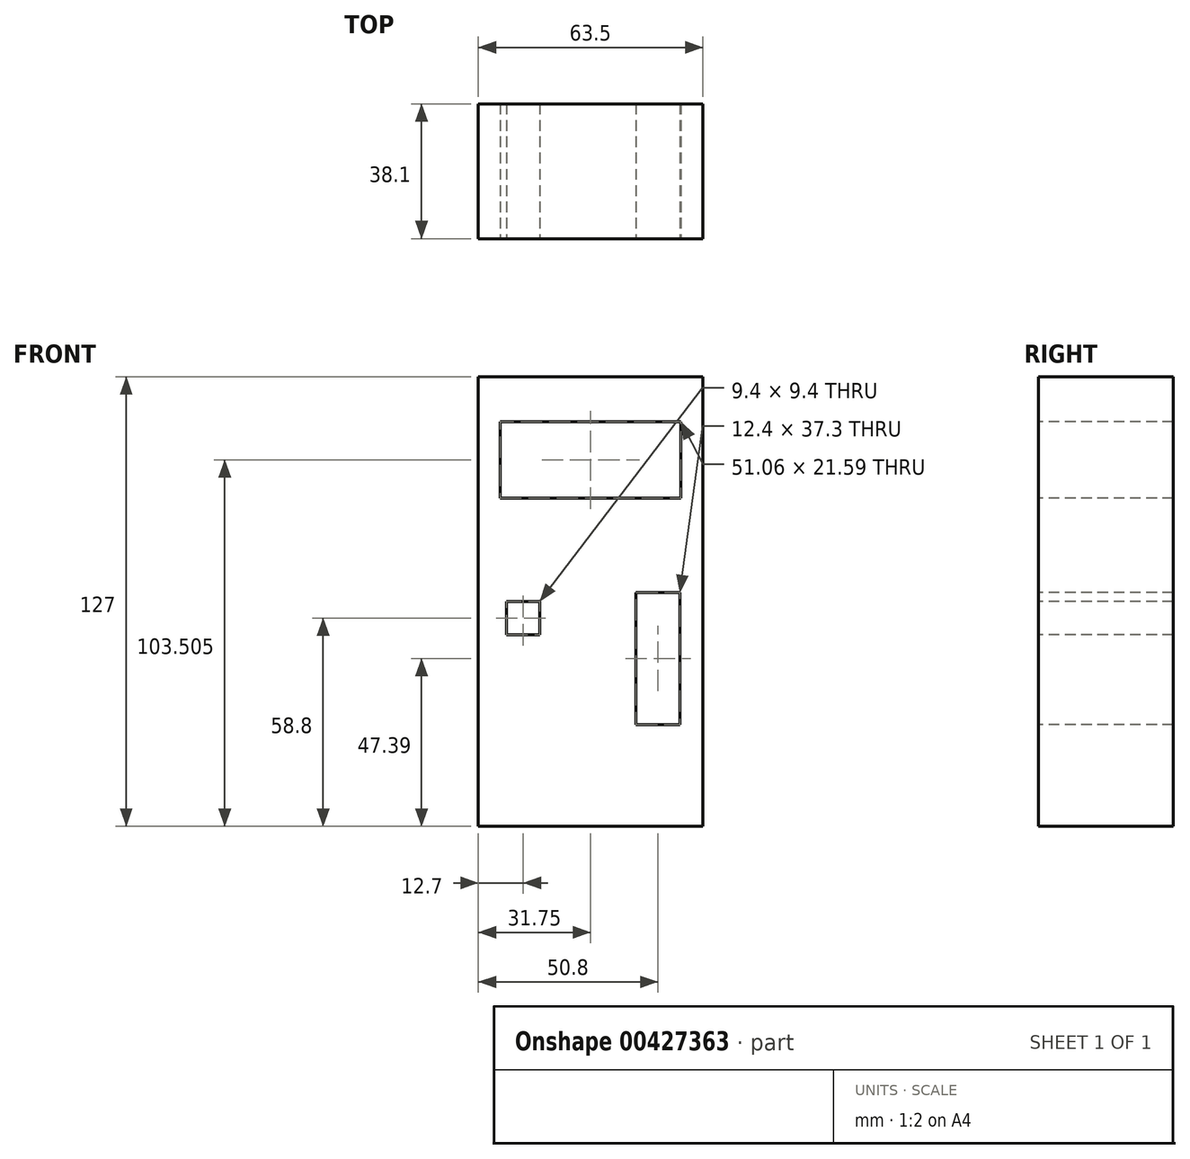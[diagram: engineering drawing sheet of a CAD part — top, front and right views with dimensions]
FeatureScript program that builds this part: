
annotation { "Feature Type Name" : "Feature", "Feature Type Description" : "" }
export const myFeature = defineFeature(function(context is Context, id is Id, definition is map)
    precondition{}
    {
        {
            var Q0;
            Q0=qCreatedBy(makeId("Front.planeOp"),FACE);
            var sketch = newSketch(context, id + "F0", { "sketchPlane" : qUnion([Q0])});
            skLineSegment(sketch, "E0.bottom", {"start": v(-31.75, 63.5) * mm, "end": v(31.75, 63.5) * mm});
            skLineSegment(sketch, "E0.top", {"start": v(-31.75, -63.5) * mm, "end": v(31.75, -63.5) * mm});
            skLineSegment(sketch, "E0.left", {"start": v(-31.75, 63.5) * mm, "end": v(-31.75, -63.5) * mm});
            skLineSegment(sketch, "E0.right", {"start": v(31.75, 63.5) * mm, "end": v(31.75, -63.5) * mm});
            skLineSegment(sketch, "E1.bottom", {"start": v(-25.53, 50.8) * mm, "end": v(25.53, 50.8) * mm});
            skLineSegment(sketch, "E1.top", {"start": v(-25.53, 29.21) * mm, "end": v(25.53, 29.21) * mm});
            skLineSegment(sketch, "E1.left", {"start": v(-25.53, 50.8) * mm, "end": v(-25.53, 29.21) * mm});
            skLineSegment(sketch, "E1.right", {"start": v(25.53, 50.8) * mm, "end": v(25.53, 29.21) * mm});
            skLineSegment(sketch, "E2", {"start": v(0, 63.5) * mm, "end": v(0, -63.5) * mm, "construction": true});
            skLineSegment(sketch, "E3", {"start": v(-25.53, 40) * mm, "end": v(25.53, 40) * mm, "construction": true});
            skPoint(sketch, "E4", {"position": v(0, 40) * mm});
            skLineSegment(sketch, "E5", {"start": v(19.05, -63.5) * mm, "end": v(19.05, 63.5) * mm, "construction": true});
            skLineSegment(sketch, "E6.bottom", {"start": v(-14.35, 0) * mm, "end": v(-23.75, 0) * mm});
            skLineSegment(sketch, "E6.top", {"start": v(-14.35, -9.4) * mm, "end": v(-23.75, -9.4) * mm});
            skLineSegment(sketch, "E6.left", {"start": v(-14.35, 0) * mm, "end": v(-14.35, -9.4) * mm});
            skLineSegment(sketch, "E6.right", {"start": v(-23.75, 0) * mm, "end": v(-23.75, -9.4) * mm});
            skPoint(sketch, "E6.middle", {"position": v(-19.05, -4.7) * mm});
            skLineSegment(sketch, "E7.bottom", {"start": v(12.85, 2.54) * mm, "end": v(25.25, 2.54) * mm});
            skLineSegment(sketch, "E7.top", {"start": v(12.85, -34.76) * mm, "end": v(25.25, -34.76) * mm});
            skLineSegment(sketch, "E7.left", {"start": v(12.85, 2.54) * mm, "end": v(12.85, -34.76) * mm});
            skLineSegment(sketch, "E7.right", {"start": v(25.25, 2.54) * mm, "end": v(25.25, -34.76) * mm});
            skPoint(sketch, "E7.middle", {"position": v(19.05, -16.1) * mm});
            skSolve(sketch);
        }
        {
            var Q0;
            Q0=makeQuery(id+"F0.imprint","IMPRINT",FACE,{"disambiguationData":[TD([[makeQuery(id+"F0.imprint","IMPRINT",EDGE,{"derivedFrom":sQuery(id+"F0.wireOp",EDGE,"E0.bottom")}),-1.0]])]});
            var Q1;
            Q1=makeQuery(id+"F0.imprint","IMPRINT",FACE,{"disambiguationData":[TD([[makeQuery(id+"F0.imprint","IMPRINT",EDGE,{"derivedFrom":sQuery(id+"F0.wireOp",EDGE,"E1.bottom")}),1.0]])]});
            extrude(context, id + "F1", {"entities" : qUnion([Q0, Q1]), "oppositeDirection" : true, "depth" : 1 / 203.2 * mm, "offsetDistance" : 25.4 * mm});
        }
        {
            var Q0;
            Q0=makeQuery(id+"F1.opExtrude","CAP_FACE",FACE,{"disambiguationData":[OSD([sQuery(id+"F0.wireOp",EDGE,"E0.bottom"),sQuery(id+"F0.wireOp",EDGE,"E0.top"),sQuery(id+"F0.wireOp",EDGE,"E0.left"),sQuery(id+"F0.wireOp",EDGE,"E0.right"),sQuery(id+"F0.wireOp",EDGE,"E1.bottom"),sQuery(id+"F0.wireOp",EDGE,"E1.top"),sQuery(id+"F0.wireOp",EDGE,"E1.left"),sQuery(id+"F0.wireOp",EDGE,"E1.right"),sQuery(id+"F0.wireOp",EDGE,"E6.bottom"),sQuery(id+"F0.wireOp",EDGE,"E6.top"),sQuery(id+"F0.wireOp",EDGE,"E6.left"),sQuery(id+"F0.wireOp",EDGE,"E6.right"),sQuery(id+"F0.wireOp",EDGE,"E7.bottom"),sQuery(id+"F0.wireOp",EDGE,"E7.top"),sQuery(id+"F0.wireOp",EDGE,"E7.left"),sQuery(id+"F0.wireOp",EDGE,"E7.right")])],"isStart":false});
            var sketch = newSketch(context, id + "F2", { "sketchPlane" : qUnion([Q0])});
            skLineSegment(sketch, "E8", {"start": v(-31.75, 60.42) * mm, "end": v(31.75, 60.43) * mm, "construction": true});
            skLineSegment(sketch, "E9", {"start": v(-28.68, 63.5) * mm, "end": v(-28.67, -63.5) * mm, "construction": true});
            skLineSegment(sketch, "E10", {"start": v(-31.75, -60.42) * mm, "end": v(31.75, -60.42) * mm, "construction": true});
            skLineSegment(sketch, "E11", {"start": v(28.67, 63.5) * mm, "end": v(28.68, -63.5) * mm, "construction": true});
            skLineSegment(sketch, "E12", {"start": v(21.75, -60.42) * mm, "end": v(21.75, -63.5) * mm, "construction": true});
            skLineSegment(sketch, "E13", {"start": v(28.68, -53.5) * mm, "end": v(31.75, -53.5) * mm, "construction": true});
            skLineSegment(sketch, "E14", {"start": v(-21.75, -60.42) * mm, "end": v(-21.75, -63.5) * mm, "construction": true});
            skLineSegment(sketch, "E15", {"start": v(-31.75, -53.5) * mm, "end": v(-28.67, -53.5) * mm, "construction": true});
            skLineSegment(sketch, "E16", {"start": v(28.67, 53.5) * mm, "end": v(31.75, 53.5) * mm, "construction": true});
            skLineSegment(sketch, "E17", {"start": v(21.75, 63.5) * mm, "end": v(21.75, 60.43) * mm, "construction": true});
            skLineSegment(sketch, "E18", {"start": v(-21.75, 63.5) * mm, "end": v(-21.75, 60.42) * mm, "construction": true});
            skLineSegment(sketch, "E19", {"start": v(-31.75, 53.5) * mm, "end": v(-28.68, 53.5) * mm, "construction": true});
            skLineSegment(sketch, "E20", {"start": v(-7.25, 63.5) * mm, "end": v(-7.25, 60.42) * mm, "construction": true});
            skLineSegment(sketch, "E21", {"start": v(7.25, 63.5) * mm, "end": v(7.25, 60.42) * mm, "construction": true});
            skLineSegment(sketch, "E22", {"start": v(-21.75, 61.96) * mm, "end": v(-7.25, 61.96) * mm, "construction": true});
            skLineSegment(sketch, "E23", {"start": v(-7.25, 61.96) * mm, "end": v(7.25, 61.96) * mm, "construction": true});
            skLineSegment(sketch, "E24", {"start": v(7.25, 61.96) * mm, "end": v(21.75, 61.96) * mm, "construction": true});
            skLineSegment(sketch, "E25", {"start": v(-7.25, -60.42) * mm, "end": v(-7.25, -63.5) * mm, "construction": true});
            skLineSegment(sketch, "E26", {"start": v(7.25, -60.42) * mm, "end": v(7.25, -63.5) * mm, "construction": true});
            skLineSegment(sketch, "E27", {"start": v(-21.75, -61.96) * mm, "end": v(-7.25, -61.96) * mm, "construction": true});
            skLineSegment(sketch, "E28", {"start": v(-7.25, -61.96) * mm, "end": v(7.25, -61.96) * mm, "construction": true});
            skLineSegment(sketch, "E29", {"start": v(7.25, -61.96) * mm, "end": v(21.75, -61.96) * mm, "construction": true});
            skLineSegment(sketch, "E30", {"start": v(-31.75, 32.1) * mm, "end": v(-28.68, 32.1) * mm, "construction": true});
            skLineSegment(sketch, "E31", {"start": v(-31.75, 10.7) * mm, "end": v(-28.67, 10.7) * mm, "construction": true});
            skLineSegment(sketch, "E32", {"start": v(-31.75, -10.7) * mm, "end": v(-28.67, -10.7) * mm, "construction": true});
            skLineSegment(sketch, "E33", {"start": v(-31.75, -32.1) * mm, "end": v(-28.67, -32.1) * mm, "construction": true});
            skLineSegment(sketch, "E34", {"start": v(-30.21, 53.5) * mm, "end": v(-30.21, 32.1) * mm, "construction": true});
            skLineSegment(sketch, "E35", {"start": v(-30.21, 32.1) * mm, "end": v(-30.21, 10.7) * mm, "construction": true});
            skLineSegment(sketch, "E36", {"start": v(-30.21, 10.7) * mm, "end": v(-30.21, -10.7) * mm, "construction": true});
            skLineSegment(sketch, "E37", {"start": v(-30.21, -10.7) * mm, "end": v(-30.21, -32.1) * mm, "construction": true});
            skLineSegment(sketch, "E38", {"start": v(-30.21, -32.1) * mm, "end": v(-30.21, -53.5) * mm, "construction": true});
            skLineSegment(sketch, "E39", {"start": v(28.67, 32.1) * mm, "end": v(31.75, 32.1) * mm, "construction": true});
            skLineSegment(sketch, "E40", {"start": v(28.68, 10.7) * mm, "end": v(31.75, 10.7) * mm, "construction": true});
            skLineSegment(sketch, "E41", {"start": v(28.68, -10.7) * mm, "end": v(31.75, -10.7) * mm, "construction": true});
            skLineSegment(sketch, "E42", {"start": v(28.68, -32.1) * mm, "end": v(31.75, -32.1) * mm, "construction": true});
            skLineSegment(sketch, "E43", {"start": v(30.21, 53.5) * mm, "end": v(30.21, 32.1) * mm, "construction": true});
            skLineSegment(sketch, "E44", {"start": v(30.21, 32.1) * mm, "end": v(30.21, 10.7) * mm, "construction": true});
            skLineSegment(sketch, "E45", {"start": v(30.21, 10.7) * mm, "end": v(30.21, -10.7) * mm, "construction": true});
            skLineSegment(sketch, "E46", {"start": v(30.21, -10.7) * mm, "end": v(30.21, -32.1) * mm, "construction": true});
            skLineSegment(sketch, "E47", {"start": v(30.21, -32.1) * mm, "end": v(30.21, -53.5) * mm, "construction": true});
            skLineSegment(sketch, "E48", {"start": v(-31.75, 53.4) * mm, "end": v(-28.68, 53.4) * mm});
            skLineSegment(sketch, "E49", {"start": v(-28.68, 53.4) * mm, "end": v(-28.68, 60.42) * mm});
            skLineSegment(sketch, "E50", {"start": v(-28.68, 60.42) * mm, "end": v(-21.65, 60.42) * mm});
            skLineSegment(sketch, "E51", {"start": v(-21.65, 60.42) * mm, "end": v(-21.65, 63.5) * mm});
            skLineSegment(sketch, "E52", {"start": v(-21.65, 60.42) * mm, "end": v(-7.35, 60.42) * mm});
            skLineSegment(sketch, "E53", {"start": v(-7.35, 60.42) * mm, "end": v(-7.35, 63.5) * mm});
            skLineSegment(sketch, "E54", {"start": v(-7.35, 63.5) * mm, "end": v(7.35, 63.5) * mm});
            skLineSegment(sketch, "E55", {"start": v(7.35, 63.5) * mm, "end": v(7.35, 60.42) * mm});
            skLineSegment(sketch, "E56", {"start": v(7.35, 60.42) * mm, "end": v(21.65, 60.43) * mm});
            skLineSegment(sketch, "E57", {"start": v(21.65, 60.42) * mm, "end": v(21.65, 63.5) * mm});
            skLineSegment(sketch, "E58", {"start": v(21.65, 60.43) * mm, "end": v(28.67, 60.43) * mm});
            skLineSegment(sketch, "E59", {"start": v(28.67, 60.43) * mm, "end": v(28.67, 53.4) * mm});
            skLineSegment(sketch, "E60", {"start": v(28.67, 53.4) * mm, "end": v(31.75, 53.4) * mm});
            skLineSegment(sketch, "E61", {"start": v(-21.65, 63.5) * mm, "end": v(-7.35, 63.5) * mm});
            skLineSegment(sketch, "E62", {"start": v(7.35, 63.5) * mm, "end": v(21.65, 63.5) * mm});
            skLineSegment(sketch, "E63", {"start": v(-31.75, 53.4) * mm, "end": v(-31.75, 32.2) * mm});
            skLineSegment(sketch, "E64", {"start": v(-31.75, 32.2) * mm, "end": v(-28.68, 32.2) * mm});
            skLineSegment(sketch, "E65", {"start": v(-28.68, 32.2) * mm, "end": v(-28.68, 53.4) * mm});
            skLineSegment(sketch, "E66", {"start": v(-31.75, 10.6) * mm, "end": v(-28.68, 10.6) * mm});
            skLineSegment(sketch, "E67", {"start": v(-28.68, 10.6) * mm, "end": v(-28.67, -10.6) * mm});
            skLineSegment(sketch, "E68", {"start": v(-28.67, -10.6) * mm, "end": v(-31.75, -10.6) * mm});
            skLineSegment(sketch, "E69", {"start": v(-31.75, -10.6) * mm, "end": v(-31.75, 10.6) * mm});
            skLineSegment(sketch, "E70", {"start": v(-31.75, -32.2) * mm, "end": v(-28.67, -32.2) * mm});
            skLineSegment(sketch, "E71", {"start": v(-28.67, -32.2) * mm, "end": v(-28.67, -53.4) * mm});
            skLineSegment(sketch, "E72", {"start": v(-28.67, -53.4) * mm, "end": v(-31.75, -53.4) * mm});
            skLineSegment(sketch, "E73", {"start": v(-31.75, -53.4) * mm, "end": v(-31.75, -32.2) * mm});
            skLineSegment(sketch, "E74.top", {"start": v(28.67, 32.2) * mm, "end": v(31.75, 32.2) * mm});
            skLineSegment(sketch, "E74.left", {"start": v(28.67, 53.4) * mm, "end": v(28.67, 32.2) * mm});
            skLineSegment(sketch, "E74.right", {"start": v(31.75, 53.4) * mm, "end": v(31.75, 32.2) * mm});
            skLineSegment(sketch, "E75.bottom", {"start": v(28.68, 10.6) * mm, "end": v(31.75, 10.6) * mm});
            skLineSegment(sketch, "E75.top", {"start": v(28.68, -10.6) * mm, "end": v(31.75, -10.6) * mm});
            skLineSegment(sketch, "E75.left", {"start": v(28.68, 10.6) * mm, "end": v(28.68, -10.6) * mm});
            skLineSegment(sketch, "E75.right", {"start": v(31.75, 10.6) * mm, "end": v(31.75, -10.6) * mm});
            skLineSegment(sketch, "E76.bottom", {"start": v(28.68, -32.2) * mm, "end": v(31.75, -32.2) * mm});
            skLineSegment(sketch, "E76.top", {"start": v(28.68, -53.4) * mm, "end": v(31.75, -53.4) * mm});
            skLineSegment(sketch, "E76.left", {"start": v(28.68, -32.2) * mm, "end": v(28.68, -53.4) * mm});
            skLineSegment(sketch, "E76.right", {"start": v(31.75, -32.2) * mm, "end": v(31.75, -53.4) * mm});
            skLineSegment(sketch, "E77.bottom", {"start": v(-21.65, -63.5) * mm, "end": v(-7.35, -63.5) * mm});
            skLineSegment(sketch, "E77.top", {"start": v(-21.65, -60.42) * mm, "end": v(-7.35, -60.42) * mm});
            skLineSegment(sketch, "E77.left", {"start": v(-21.65, -63.5) * mm, "end": v(-21.65, -60.43) * mm});
            skLineSegment(sketch, "E77.right", {"start": v(-7.35, -63.5) * mm, "end": v(-7.35, -60.43) * mm});
            skLineSegment(sketch, "E78.bottom", {"start": v(7.35, -60.42) * mm, "end": v(21.65, -60.42) * mm});
            skLineSegment(sketch, "E78.top", {"start": v(7.35, -63.5) * mm, "end": v(21.65, -63.5) * mm});
            skLineSegment(sketch, "E78.left", {"start": v(7.35, -60.42) * mm, "end": v(7.35, -63.5) * mm});
            skLineSegment(sketch, "E78.right", {"start": v(21.65, -60.42) * mm, "end": v(21.65, -63.5) * mm});
            skSolve(sketch);
        }
        {
            var Q0;
            Q0=makeQuery(id+"F2.imprint","IMPRINT",FACE,{"disambiguationData":[TD([[makeQuery(id+"F2.imprint","IMPRINT",EDGE,{"derivedFrom":sQuery(id+"F2.wireOp",EDGE,"E55")}),1.0]])]});
            var Q1;
            Q1=makeQuery(id+"F2.imprint","IMPRINT",FACE,{"disambiguationData":[TD([[makeQuery(id+"F2.imprint","IMPRINT",EDGE,{"derivedFrom":sQuery(id+"F2.wireOp",EDGE,"E51")}),-1.0]])]});
            var Q2;
            Q2=makeQuery(id+"F2.imprint","IMPRINT",FACE,{"disambiguationData":[TD([[makeQuery(id+"F2.imprint","IMPRINT",EDGE,{"derivedFrom":sQuery(id+"F2.wireOp",EDGE,"E70")}),-1.0]])]});
            var Q3;
            Q3=makeQuery(id+"F2.imprint","IMPRINT",FACE,{"disambiguationData":[TD([[makeQuery(id+"F2.imprint","IMPRINT",EDGE,{"derivedFrom":sQuery(id+"F2.wireOp",EDGE,"E66")}),-1.0]])]});
            var Q4;
            Q4=makeQuery(id+"F2.imprint","IMPRINT",FACE,{"disambiguationData":[TD([[makeQuery(id+"F2.imprint","IMPRINT",EDGE,{"derivedFrom":sQuery(id+"F2.wireOp",EDGE,"E48")}),-1.0]])]});
            var Q5;
            Q5=makeQuery(id+"F2.imprint","IMPRINT",FACE,{"disambiguationData":[TD([[makeQuery(id+"F2.imprint","IMPRINT",EDGE,{"derivedFrom":sQuery(id+"F2.wireOp",EDGE,"E76.bottom")}),-1.0]])]});
            var Q6;
            Q6=makeQuery(id+"F2.imprint","IMPRINT",FACE,{"disambiguationData":[TD([[makeQuery(id+"F2.imprint","IMPRINT",EDGE,{"derivedFrom":sQuery(id+"F2.wireOp",EDGE,"E75.bottom")}),-1.0]])]});
            var Q7;
            Q7=makeQuery(id+"F2.imprint","IMPRINT",FACE,{"disambiguationData":[TD([[makeQuery(id+"F2.imprint","IMPRINT",EDGE,{"derivedFrom":sQuery(id+"F2.wireOp",EDGE,"E60")}),-1.0]])]});
            var Q8;
            Q8=makeQuery(id+"F2.imprint","IMPRINT",FACE,{"disambiguationData":[TD([[makeQuery(id+"F2.imprint","IMPRINT",EDGE,{"derivedFrom":sQuery(id+"F2.wireOp",EDGE,"E77.bottom")}),-1.0]])]});
            var Q9;
            Q9=makeQuery(id+"F2.imprint","IMPRINT",FACE,{"disambiguationData":[TD([[makeQuery(id+"F2.imprint","IMPRINT",EDGE,{"derivedFrom":sQuery(id+"F2.wireOp",EDGE,"E78.bottom")}),-1.0]])]});
            extrude(context, id + "F3", {"entities" : qUnion([Q0, Q1, Q2, Q3, Q4, Q5, Q6, Q7, Q8, Q9]), "operationType" : NewBodyOperationType.REMOVE, "oppositeDirection" : true, "depth" : 25 * mm, "offsetDistance" : 25 * mm});
        }
        {
            var Q0;
            Q0=makeQuery(id+"F0.imprint","IMPRINT",FACE,{"disambiguationData":[TD([[makeQuery(id+"F0.imprint","IMPRINT",EDGE,{"derivedFrom":sQuery(id+"F0.wireOp",EDGE,"E0.bottom")}),-1.0]])]});
            extrude(context, id + "F4", {"entities" : qUnion([Q0]), "operationType" : NewBodyOperationType.ADD, "oppositeDirection" : true, "depth" : 38.1 * mm, "offsetDistance" : 25.4 * mm});
        }
    });
